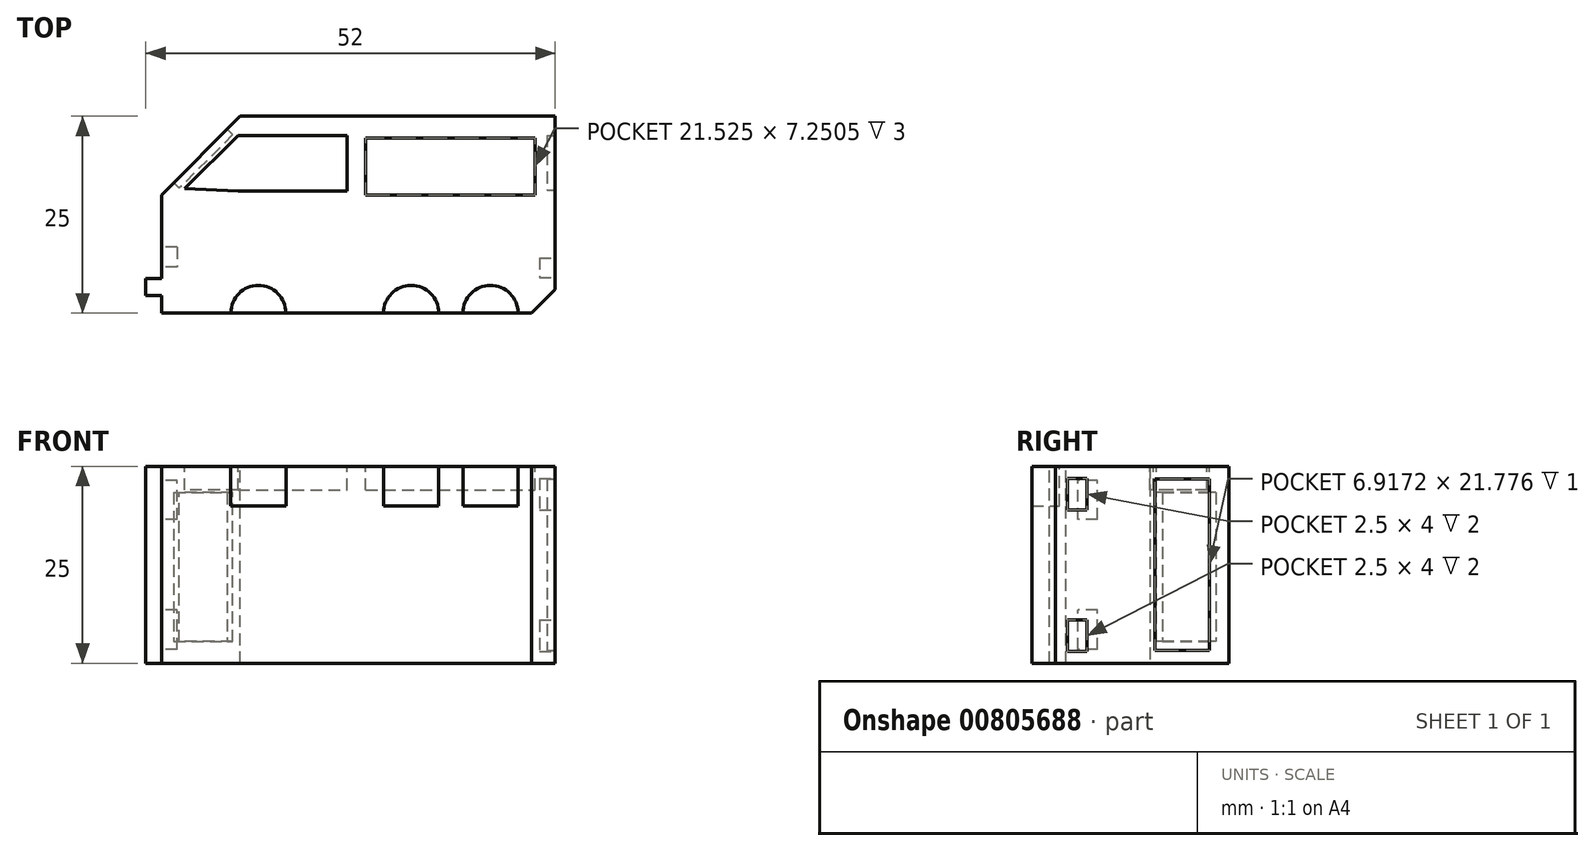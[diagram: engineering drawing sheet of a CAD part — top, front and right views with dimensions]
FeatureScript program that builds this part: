
annotation { "Feature Type Name" : "Feature", "Feature Type Description" : "" }
export const myFeature = defineFeature(function(context is Context, id is Id, definition is map)
    precondition{}
    {
        {
            var Q0;
            Q0=qCreatedBy(makeId("Top.planeOp"),FACE);
            var sketch = newSketch(context, id + "F0", { "sketchPlane" : qUnion([Q0])});
            skLineSegment(sketch, "E0.bottom", {"start": v(-23.6, 4.63) * mm, "end": v(26.4, 4.63) * mm});
            skLineSegment(sketch, "E0.top", {"start": v(-23.6, -20.37) * mm, "end": v(26.4, -20.37) * mm});
            skLineSegment(sketch, "E0.left", {"start": v(-23.6, 4.63) * mm, "end": v(-23.6, -20.37) * mm});
            skLineSegment(sketch, "E0.right", {"start": v(26.4, 4.63) * mm, "end": v(26.4, -20.37) * mm});
            skSolve(sketch);
        }
        {
            var Q0;
            Q0 = qSketchRegion(id + "F0", true);
            extrude(context, id + "F1", {"entities" : qUnion([Q0]), "endBound" : BoundingType.SYMMETRIC, "depth" : 25 * mm, "offsetDistance" : 25 * mm});
        }
        {
            var Q0;
            Q0=makeQuery(id+"F1.opExtrude","CAP_FACE",FACE,{"disambiguationData":[OSD([sQuery(id+"F0.wireOp",EDGE,"E0.bottom"),sQuery(id+"F0.wireOp",EDGE,"E0.top"),sQuery(id+"F0.wireOp",EDGE,"E0.left"),sQuery(id+"F0.wireOp",EDGE,"E0.right")])],"isStart":false});
            var sketch = newSketch(context, id + "F2", { "sketchPlane" : qUnion([Q0])});
            skCircle(sketch, "E1", {"center": v(-11.29, -20.37) * mm, "radius": 3.5 * mm});
            skCircle(sketch, "E2", {"center": v(8.12, -20.37) * mm, "radius": 3.5 * mm});
            skCircle(sketch, "E3", {"center": v(18.2, -20.37) * mm, "radius": 3.5 * mm});
            skSolve(sketch);
        }
        {
            var Q0;
            Q0 = qSketchRegion(id + "F2", true);
            extrude(context, id + "F3", {"entities" : qUnion([Q0]), "operationType" : NewBodyOperationType.REMOVE, "oppositeDirection" : true, "depth" : 5 * mm, "offsetDistance" : 25 * mm});
        }
        {
            var Q0;
            Q0=makeQuery(id+"F1.opExtrude","SWEPT_EDGE",EDGE,{"disambiguationData":[OSD([sQuery(id+"F0.wireOp",EDGE,"E0.bottom"),sQuery(id+"F0.wireOp",EDGE,"E0.left")])]});
            chamfer(context, id + "F4", {"entities" : qUnion([Q0]), "width" : 10 * mm, "tangentPropagation" : true});
        }
        {
            var Q0;
            Q0=makeQuery(id+"F1.opExtrude","SWEPT_EDGE",EDGE,{"disambiguationData":[OSD([sQuery(id+"F0.wireOp",EDGE,"E0.top"),sQuery(id+"F0.wireOp",EDGE,"E0.right")])]});
            chamfer(context, id + "F5", {"entities" : qUnion([Q0]), "width" : 3 * mm, "tangentPropagation" : true});
        }
        {
            var Q0;
            Q0=makeQuery(id+"F1.opExtrude","SWEPT_FACE",FACE,{"disambiguationData":[OSD([sQuery(id+"F0.wireOp",EDGE,"E0.left")])]});
            var sketch = newSketch(context, id + "F6", { "sketchPlane" : qUnion([Q0])});
            skLineSegment(sketch, "E4.bottom", {"start": v(16.02, -12.5) * mm, "end": v(18.14, -12.5) * mm});
            skLineSegment(sketch, "E4.top", {"start": v(16.02, 12.5) * mm, "end": v(18.14, 12.5) * mm});
            skLineSegment(sketch, "E4.left", {"start": v(16.02, -12.5) * mm, "end": v(16.02, 12.5) * mm});
            skLineSegment(sketch, "E4.right", {"start": v(18.14, -12.5) * mm, "end": v(18.14, 12.5) * mm});
            skSolve(sketch);
        }
        {
            var Q0;
            Q0 = qSketchRegion(id + "F6", true);
            extrude(context, id + "F7", {"entities" : qUnion([Q0]), "operationType" : NewBodyOperationType.ADD, "depth" : 2 * mm, "offsetDistance" : 25 * mm});
        }
        {
            var Q0;
            Q0=makeQuery(id+"F4.opChamfer","BLEND_FACE",FACE,{"disambiguationData":[OSD([sQuery(id+"F0.wireOp",EDGE,"E0.bottom"),sQuery(id+"F0.wireOp",EDGE,"E0.left")])]});
            var sketch = newSketch(context, id + "F8", { "sketchPlane" : qUnion([Q0])});
            skLineSegment(sketch, "E5.bottom", {"start": v(8.67, -9.74) * mm, "end": v(18.28, -9.74) * mm});
            skLineSegment(sketch, "E5.top", {"start": v(8.67, 9.18) * mm, "end": v(18.28, 9.18) * mm});
            skLineSegment(sketch, "E5.left", {"start": v(8.67, -9.74) * mm, "end": v(8.67, 9.18) * mm});
            skLineSegment(sketch, "E5.right", {"start": v(18.28, -9.74) * mm, "end": v(18.28, 9.18) * mm});
            skSolve(sketch);
        }
        {
            var Q0;
            Q0 = qSketchRegion(id + "F8", true);
            extrude(context, id + "F9", {"entities" : qUnion([Q0]), "operationType" : NewBodyOperationType.REMOVE, "endBound" : BoundingType.SYMMETRIC, "depth" : 2 * mm, "offsetDistance" : 25 * mm});
        }
        {
            var Q0;
            Q0=makeQuery(id+"F7.boolean.opBoolean","MERGE",FACE,{"derivedFrom":[makeQuery(id+"F1.opExtrude","CAP_FACE",FACE,{"disambiguationData":[OSD([sQuery(id+"F0.wireOp",EDGE,"E0.bottom"),sQuery(id+"F0.wireOp",EDGE,"E0.top"),sQuery(id+"F0.wireOp",EDGE,"E0.left"),sQuery(id+"F0.wireOp",EDGE,"E0.right")])],"isStart":false}),makeQuery(id+"F7.opExtrude","SWEPT_FACE",FACE,{"disambiguationData":[OSD([sQuery(id+"F6.wireOp",EDGE,"E4.top")])]})]});
            var sketch = newSketch(context, id + "F10", { "sketchPlane" : qUnion([Q0])});
            skLineSegment(sketch, "E6.bottom", {"start": v(-13.88, 2.2) * mm, "end": v(0, 2.2) * mm});
            skLineSegment(sketch, "E6.top", {"start": v(-13.88, -4.9) * mm, "end": v(0, -4.9) * mm});
            skLineSegment(sketch, "E6.left", {"start": v(-13.88, 2.2) * mm, "end": v(-13.88, -4.9) * mm});
            skLineSegment(sketch, "E6.right", {"start": v(0, 2.2) * mm, "end": v(0, -4.9) * mm});
            skLineSegment(sketch, "E7.bottom", {"start": v(2.36, 1.88) * mm, "end": v(23.88, 1.88) * mm});
            skLineSegment(sketch, "E7.top", {"start": v(2.36, -5.37) * mm, "end": v(23.88, -5.37) * mm});
            skLineSegment(sketch, "E7.left", {"start": v(2.36, 1.88) * mm, "end": v(2.36, -5.37) * mm});
            skLineSegment(sketch, "E7.right", {"start": v(23.88, 1.88) * mm, "end": v(23.88, -5.37) * mm});
            skLineSegment(sketch, "E8", {"start": v(-13.88, 2.2) * mm, "end": v(-20.63, -4.55) * mm});
            skLineSegment(sketch, "E9", {"start": v(-13.88, -4.9) * mm, "end": v(-20.63, -4.55) * mm});
            skSolve(sketch);
        }
        {
            var Q0;
            Q0 = qSketchRegion(id + "F10", true);
            extrude(context, id + "F11", {"entities" : qUnion([Q0]), "operationType" : NewBodyOperationType.REMOVE, "oppositeDirection" : true, "depth" : 3 * mm, "offsetDistance" : 25 * mm});
        }
        {
            var Q0;
            Q0=makeQuery(id+"F1.opExtrude","SWEPT_FACE",FACE,{"disambiguationData":[OSD([sQuery(id+"F0.wireOp",EDGE,"E0.right")])]});
            var sketch = newSketch(context, id + "F12", { "sketchPlane" : qUnion([Q0])});
            skLineSegment(sketch, "E10.bottom", {"start": v(2.2, 10.89) * mm, "end": v(-4.73, 10.89) * mm});
            skLineSegment(sketch, "E10.top", {"start": v(2.2, -10.89) * mm, "end": v(-4.73, -10.89) * mm});
            skLineSegment(sketch, "E10.left", {"start": v(2.2, 10.89) * mm, "end": v(2.2, -10.89) * mm});
            skLineSegment(sketch, "E10.right", {"start": v(-4.73, 10.89) * mm, "end": v(-4.73, -10.89) * mm});
            skSolve(sketch);
        }
        {
            var Q0;
            Q0 = qSketchRegion(id + "F12", true);
            extrude(context, id + "F13", {"entities" : qUnion([Q0]), "operationType" : NewBodyOperationType.REMOVE, "endBound" : BoundingType.SYMMETRIC, "oppositeDirection" : true, "depth" : 2 * mm, "offsetDistance" : 25 * mm});
        }
        {
            var Q0;
            Q0=makeQuery(id+"F1.opExtrude","SWEPT_FACE",FACE,{"disambiguationData":[OSD([sQuery(id+"F0.wireOp",EDGE,"E0.right")])]});
            var sketch = newSketch(context, id + "F14", { "sketchPlane" : qUnion([Q0])});
            skLineSegment(sketch, "E11.bottom", {"start": v(-13.37, -7) * mm, "end": v(-15.87, -7) * mm});
            skLineSegment(sketch, "E11.top", {"start": v(-13.37, -11) * mm, "end": v(-15.87, -11) * mm});
            skLineSegment(sketch, "E11.left", {"start": v(-13.37, -7) * mm, "end": v(-13.37, -11) * mm});
            skLineSegment(sketch, "E11.right", {"start": v(-15.87, -7) * mm, "end": v(-15.87, -11) * mm});
            skLineSegment(sketch, "E12.bottom", {"start": v(-11.87, 11) * mm, "end": v(-13.37, 11) * mm});
            skLineSegment(sketch, "E12.top", {"start": v(-13.37, 7) * mm, "end": v(-15.87, 7) * mm});
            skLineSegment(sketch, "E12.left", {"start": v(-13.37, 11) * mm, "end": v(-13.37, 7) * mm});
            skLineSegment(sketch, "E12.right", {"start": v(-15.87, 11) * mm, "end": v(-15.87, 7) * mm});
            skLineSegment(sketch, "E13", {"start": v(-15.87, 11) * mm, "end": v(-13.37, 11) * mm});
            skSolve(sketch);
        }
        {
            var Q0;
            Q0 = qSketchRegion(id + "F14", true);
            extrude(context, id + "F15", {"entities" : qUnion([Q0]), "operationType" : NewBodyOperationType.REMOVE, "oppositeDirection" : true, "depth" : 2 * mm, "offsetDistance" : 25 * mm});
        }
        {
            var Q0;
            {var subQ0=sQuery(id+"F0.wireOp",EDGE,"E0.left");Q0=makeQuery(id+"F7.boolean.opBoolean","SPLIT",FACE,{"disambiguationData":[TD([makeQuery(id+"F7.opExtrude","SWEPT_FACE",FACE,{"disambiguationData":[OSD([sQuery(id+"F6.wireOp",EDGE,"E4.left")])]})])],"derivedFrom":makeQuery(id+"F1.opExtrude","SWEPT_FACE",FACE,{"disambiguationData":[OSD([subQ0])]})});}
            var sketch = newSketch(context, id + "F16", { "sketchPlane" : qUnion([Q0])});
            skLineSegment(sketch, "E14.bottom", {"start": v(12.02, 5.75) * mm, "end": v(14.52, 5.75) * mm});
            skLineSegment(sketch, "E14.top", {"start": v(12.02, 10.75) * mm, "end": v(14.52, 10.75) * mm});
            skLineSegment(sketch, "E14.left", {"start": v(12.02, 5.75) * mm, "end": v(12.02, 10.75) * mm});
            skLineSegment(sketch, "E14.right", {"start": v(14.52, 5.75) * mm, "end": v(14.52, 10.75) * mm});
            skLineSegment(sketch, "E15.bottom", {"start": v(12.02, -10.75) * mm, "end": v(14.52, -10.75) * mm});
            skLineSegment(sketch, "E15.top", {"start": v(12.02, -5.75) * mm, "end": v(14.52, -5.75) * mm});
            skLineSegment(sketch, "E15.left", {"start": v(12.02, -10.75) * mm, "end": v(12.02, -5.75) * mm});
            skLineSegment(sketch, "E15.right", {"start": v(14.52, -10.75) * mm, "end": v(14.52, -5.75) * mm});
            skSolve(sketch);
        }
        {
            var Q0;
            Q0 = qSketchRegion(id + "F16", true);
            extrude(context, id + "F17", {"entities" : qUnion([Q0]), "operationType" : NewBodyOperationType.REMOVE, "oppositeDirection" : true, "depth" : 2 * mm, "offsetDistance" : 25 * mm});
        }
    });
